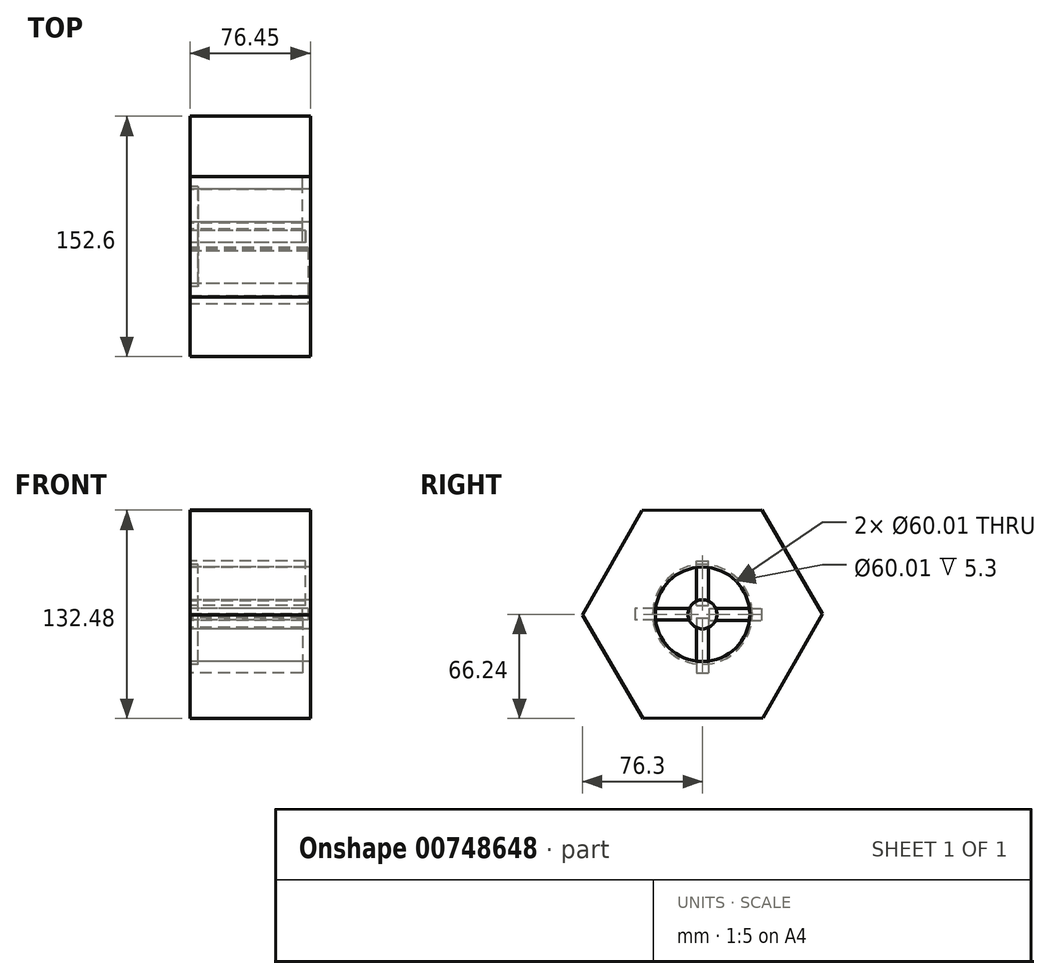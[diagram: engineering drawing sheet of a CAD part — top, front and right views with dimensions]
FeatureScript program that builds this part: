
annotation { "Feature Type Name" : "Feature", "Feature Type Description" : "" }
export const myFeature = defineFeature(function(context is Context, id is Id, definition is map)
    precondition{}
    {
        {
            var Q0;
            Q0=qCreatedBy(makeId("Right.planeOp"),FACE);
            var sketch = newSketch(context, id + "F0", { "sketchPlane" : qUnion([Q0])});
            skCircle(sketch, "E0.cCircle", {"center": v(0, 0) * mm, "radius": 66.08 * mm, "construction": true});
            skLineSegment(sketch, "E0.0", {"start": v(76.3, 0.33) * mm, "end": v(38.43, -65.92) * mm});
            skLineSegment(sketch, "E0.1", {"start": v(38.43, -65.92) * mm, "end": v(-37.87, -66.24) * mm});
            skLineSegment(sketch, "E0.2", {"start": v(-37.87, -66.24) * mm, "end": v(-76.3, -0.33) * mm});
            skLineSegment(sketch, "E0.3", {"start": v(-76.3, -0.33) * mm, "end": v(-38.43, 65.92) * mm});
            skLineSegment(sketch, "E0.4", {"start": v(-38.43, 65.92) * mm, "end": v(37.87, 66.24) * mm});
            skLineSegment(sketch, "E0.5", {"start": v(37.87, 66.24) * mm, "end": v(76.3, 0.33) * mm});
            skPoint(sketch, "E0.0.midPoint", {"position": v(57.37, -32.8) * mm});
            skSolve(sketch);
        }
        {
            var Q0;
            Q0=makeQuery(id+"F0.imprint","IMPRINT",FACE,{"disambiguationData":[TD([[makeQuery(id+"F0.imprint","IMPRINT",EDGE,{"derivedFrom":sQuery(id+"F0.wireOp",EDGE,"E0.0")}),-1.0]])]});
            extrude(context, id + "F1", {"entities" : qUnion([Q0]), "depth" : 76.45 * mm, "offsetDistance" : 25.4 * mm});
        }
        {
            var Q0;
            Q0=qCreatedBy(makeId("Right.planeOp"),FACE);
            var sketch = newSketch(context, id + "F2", { "sketchPlane" : qUnion([Q0])});
            skCircle(sketch, "E1", {"center": v(0, 0) * mm, "radius": 30 * mm});
            skCircle(sketch, "E2", {"center": v(0, 0) * mm, "radius": 9.2 * mm});
            skSolve(sketch);
        }
        {
            var Q0;
            Q0=makeQuery(id+"F2.imprint","IMPRINT",FACE,{"disambiguationData":[TD([[makeQuery(id+"F2.imprint","IMPRINT",EDGE,{"derivedFrom":sQuery(id+"F2.wireOp",EDGE,"E1")}),1.0]])]});
            extrude(context, id + "F3", {"entities" : qUnion([Q0]), "operationType" : NewBodyOperationType.REMOVE, "depth" : 91.7 * mm, "offsetDistance" : 25.4 * mm});
        }
        {
            var Q0;
            Q0=qCreatedBy(makeId("Right.planeOp"),FACE);
            var sketch = newSketch(context, id + "F4", { "sketchPlane" : qUnion([Q0])});
            skLineSegment(sketch, "E3.bottom", {"start": v(-7.2, 3.67) * mm, "end": v(-42.94, 3.67) * mm});
            skLineSegment(sketch, "E3.top", {"start": v(-7.2, -3.67) * mm, "end": v(-42.94, -3.67) * mm});
            skLineSegment(sketch, "E3.left", {"start": v(-7.2, 3.67) * mm, "end": v(-7.2, -3.67) * mm});
            skLineSegment(sketch, "E3.right", {"start": v(-42.94, 3.67) * mm, "end": v(-42.94, -3.67) * mm});
            skPoint(sketch, "E3.middle", {"position": v(-25.07, 0) * mm});
            skSolve(sketch);
        }
        {
            var Q0;
            Q0=makeQuery(id+"F4.imprint","IMPRINT",FACE,{"disambiguationData":[TD([[makeQuery(id+"F4.imprint","IMPRINT",EDGE,{"derivedFrom":sQuery(id+"F4.wireOp",EDGE,"E3.bottom")}),1.0]])]});
            extrude(context, id + "F5", {"entities" : qUnion([Q0]), "depth" : 75.18 * mm, "offsetDistance" : 25.4 * mm});
        }
        {
            var Q0;
            Q0=qCreatedBy(makeId("Right.planeOp"),FACE);
            var sketch = newSketch(context, id + "F6", { "sketchPlane" : qUnion([Q0])});
            skLineSegment(sketch, "E4.bottom", {"start": v(-3.76, 5.79) * mm, "end": v(3.76, 5.79) * mm});
            skLineSegment(sketch, "E4.top", {"start": v(-3.76, 33.81) * mm, "end": v(3.76, 33.81) * mm});
            skLineSegment(sketch, "E4.left", {"start": v(-3.76, 5.79) * mm, "end": v(-3.76, 33.81) * mm});
            skLineSegment(sketch, "E4.right", {"start": v(3.76, 5.79) * mm, "end": v(3.76, 33.81) * mm});
            skPoint(sketch, "E4.middle", {"position": v(0, 19.8) * mm});
            skSolve(sketch);
        }
        {
            var Q0;
            Q0=makeQuery(id+"F6.imprint","IMPRINT",FACE,{"disambiguationData":[TD([[makeQuery(id+"F6.imprint","IMPRINT",EDGE,{"derivedFrom":sQuery(id+"F6.wireOp",EDGE,"E4.bottom")}),1.0]])]});
            extrude(context, id + "F7", {"entities" : qUnion([Q0]), "depth" : 73.4 * mm, "offsetDistance" : 25.4 * mm});
        }
        {
            var Q0;
            Q0=qCreatedBy(makeId("Right.planeOp"),FACE);
            var sketch = newSketch(context, id + "F8", { "sketchPlane" : qUnion([Q0])});
            skLineSegment(sketch, "E5.bottom", {"start": v(-3.76, -2.34) * mm, "end": v(3.76, -2.34) * mm});
            skLineSegment(sketch, "E5.top", {"start": v(-3.76, -37.26) * mm, "end": v(3.76, -37.26) * mm});
            skLineSegment(sketch, "E5.left", {"start": v(-3.76, -2.34) * mm, "end": v(-3.76, -37.26) * mm});
            skLineSegment(sketch, "E5.right", {"start": v(3.76, -2.34) * mm, "end": v(3.76, -37.26) * mm});
            skPoint(sketch, "E5.middle", {"position": v(0, -19.8) * mm});
            skSolve(sketch);
        }
        {
            var Q0;
            Q0=makeQuery(id+"F8.imprint","IMPRINT",FACE,{"disambiguationData":[TD([[makeQuery(id+"F8.imprint","IMPRINT",EDGE,{"derivedFrom":sQuery(id+"F8.wireOp",EDGE,"E5.bottom")}),-1.0]])]});
            extrude(context, id + "F9", {"entities" : qUnion([Q0]), "depth" : 71.37 * mm, "offsetDistance" : 25.4 * mm});
        }
        {
            var Q0;
            Q0=qCreatedBy(makeId("Right.planeOp"),FACE);
            var sketch = newSketch(context, id + "F10", { "sketchPlane" : qUnion([Q0])});
            skLineSegment(sketch, "E6.bottom", {"start": v(4.57, -3.76) * mm, "end": v(37.87, -3.76) * mm});
            skLineSegment(sketch, "E6.top", {"start": v(4.57, 3.76) * mm, "end": v(37.87, 3.76) * mm});
            skLineSegment(sketch, "E6.left", {"start": v(4.57, -3.76) * mm, "end": v(4.57, 3.76) * mm});
            skLineSegment(sketch, "E6.right", {"start": v(37.87, -3.76) * mm, "end": v(37.87, 3.76) * mm});
            skPoint(sketch, "E6.middle", {"position": v(21.22, 0) * mm});
            skSolve(sketch);
        }
        {
            var Q0;
            Q0=makeQuery(id+"F10.imprint","IMPRINT",FACE,{"disambiguationData":[TD([[makeQuery(id+"F10.imprint","IMPRINT",EDGE,{"derivedFrom":sQuery(id+"F10.wireOp",EDGE,"E6.bottom")}),1.0]])]});
            extrude(context, id + "F11", {"entities" : qUnion([Q0]), "depth" : 71.63 * mm, "offsetDistance" : 25.4 * mm});
        }
        {
            var Q0;
            Q0=qCreatedBy(makeId("Right.planeOp"),FACE);
            var sketch = newSketch(context, id + "F12", { "sketchPlane" : qUnion([Q0])});
            skCircle(sketch, "E7", {"center": v(0, 0) * mm, "radius": 33.66 * mm});
            skSolve(sketch);
        }
        {
            var Q0;
            Q0=sQuery(id+"F12.wireOp",EDGE,"E7");
            extrude(context, id + "F13", {"bodyType" : ToolBodyType.SURFACE, "surfaceEntities" : qUnion([Q0]), "depth" : 160.6 * mm, "offsetDistance" : 25 * mm});
        }
        {
            var Q0;
            Q0=qCreatedBy(makeId("Right.planeOp"),FACE);
            var sketch = newSketch(context, id + "F14", { "sketchPlane" : qUnion([Q0])});
            skCircle(sketch, "E8", {"center": v(0, 0) * mm, "radius": 31.68 * mm});
            skSolve(sketch);
        }
        {
            var Q0;
            Q0=makeQuery(id+"F14.imprint","IMPRINT",FACE,{"disambiguationData":[TD([[makeQuery(id+"F14.imprint","IMPRINT",EDGE,{"derivedFrom":sQuery(id+"F14.wireOp",EDGE,"E8")}),1.0]])]});
            extrude(context, id + "F15", {"entities" : qUnion([Q0]), "depth" : 5.3 * mm, "offsetDistance" : 25 * mm});
        }
    });
